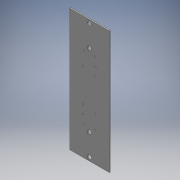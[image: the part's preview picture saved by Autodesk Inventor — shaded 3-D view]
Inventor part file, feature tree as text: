
AUTODESK INVENTOR PART (.ipt)
format: ipt  version: 2016 (Build 200138000, 138)  size: 150,528 bytes
history: native  units: mm
features: extrude x2, sketch x2, other x1
ambient origin geometry x8: Origin, YZ Plane, XZ Plane, XY Plane, X Axis, Y Axis, Z Axis, Center Point
bodies: Body1 (feature_tree)
feature tree (5):
  other  "ソリッド1"
  extrude  "押し出し1"  Depth=84.0mm
  extrude  "押し出し6"  Depth=260.0mm
  sketch  "スケッチ1"
  sketch  "スケッチ2"
